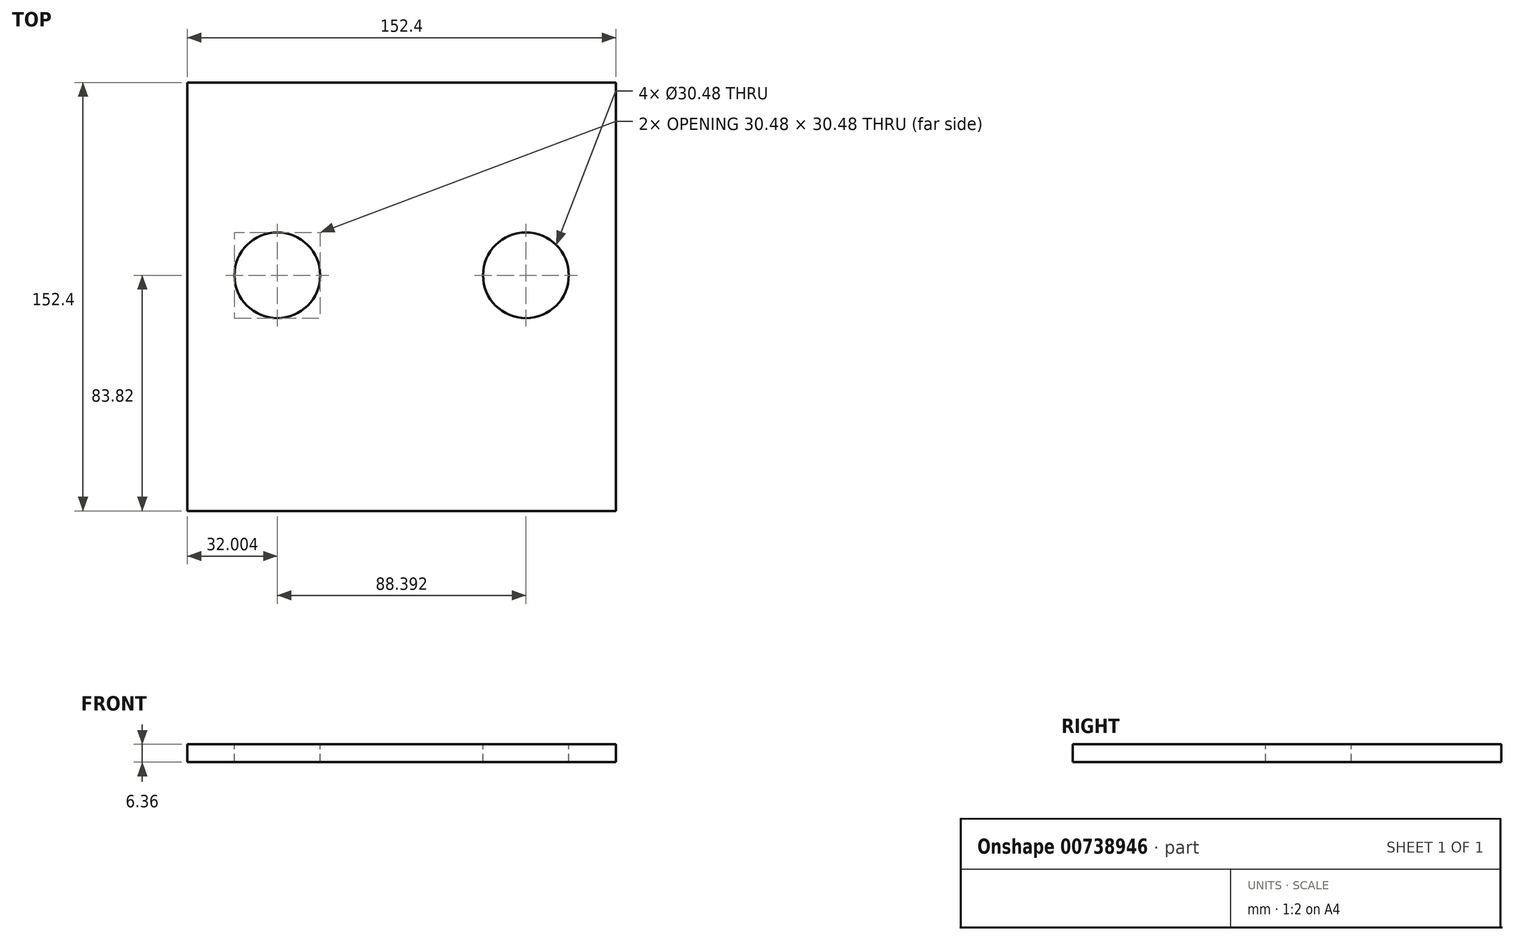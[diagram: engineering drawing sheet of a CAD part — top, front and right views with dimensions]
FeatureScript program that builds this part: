
annotation { "Feature Type Name" : "Feature", "Feature Type Description" : "" }
export const myFeature = defineFeature(function(context is Context, id is Id, definition is map)
    precondition{}
    {
        {
            var Q0;
            Q0=qCreatedBy(makeId("Front.planeOp"),FACE);
            var sketch = newSketch(context, id + "F0", { "sketchPlane" : qUnion([Q0])});
            skLineSegment(sketch, "E0.bottom", {"start": v(76.2, -3.17) * mm, "end": v(-76.2, -3.18) * mm});
            skLineSegment(sketch, "E0.top", {"start": v(76.2, 3.18) * mm, "end": v(-76.2, 3.17) * mm});
            skLineSegment(sketch, "E0.left", {"start": v(76.2, -3.17) * mm, "end": v(76.2, 3.18) * mm});
            skLineSegment(sketch, "E0.right", {"start": v(-76.2, -3.18) * mm, "end": v(-76.2, 3.17) * mm});
            skPoint(sketch, "E0.middle", {"position": v(0, 0) * mm});
            skSolve(sketch);
        }
        {
            var Q0;
            Q0=makeQuery(id+"F0.imprint","IMPRINT",FACE,{"disambiguationData":[TD([[makeQuery(id+"F0.imprint","IMPRINT",EDGE,{"derivedFrom":sQuery(id+"F0.wireOp",EDGE,"E0.bottom")}),-1.0]])]});
            extrude(context, id + "F1", {"entities" : qUnion([Q0]), "depth" : 152.4 * mm, "offsetDistance" : 25.4 * mm});
        }
        {
            var Q0;
            Q0=makeQuery(id+"F1.opExtrude","SWEPT_FACE",FACE,{"disambiguationData":[OSD([sQuery(id+"F0.wireOp",EDGE,"E0.top")])]});
            var sketch = newSketch(context, id + "F2", { "sketchPlane" : qUnion([Q0])});
            skPoint(sketch, "E1", {"position": v(-44.2, -68.58) * mm});
            skLineSegment(sketch, "E2", {"start": v(-44.2, -68.58) * mm, "end": v(-44.2, -152.4) * mm});
            skPoint(sketch, "E3", {"position": v(44.2, -68.58) * mm});
            skLineSegment(sketch, "E4", {"start": v(-44.2, -68.58) * mm, "end": v(44.2, -68.58) * mm});
            skLineSegment(sketch, "E5", {"start": v(44.2, -68.58) * mm, "end": v(44.2, -152.4) * mm});
            skLineSegment(sketch, "E6", {"start": v(-44.2, -68.58) * mm, "end": v(-76.2, -68.58) * mm});
            skLineSegment(sketch, "E7", {"start": v(44.2, -68.58) * mm, "end": v(76.2, -68.58) * mm});
            skPoint(sketch, "E8", {"position": v(0, -68.58) * mm});
            skSolve(sketch);
        }
        {
            var Q0;
            Q0=sQuery(id+"F2.wireOp",VERTEX,"E1");
            var Q1;
            Q1=sQuery(id+"F2.wireOp",VERTEX,"E3");
            var Q2;
            Q2=makeQuery(id+"F1.opExtrude","SWEPT_BODY",BODY,{"disambiguationData":[OSD([sQuery(id+"F0.wireOp",EDGE,"E0.bottom"),sQuery(id+"F0.wireOp",EDGE,"E0.top"),sQuery(id+"F0.wireOp",EDGE,"E0.left"),sQuery(id+"F0.wireOp",EDGE,"E0.right")])]});
            hole(context, id + "F3", {"style" : HoleStyle.SIMPLE, "endStyle" : HoleEndStyle.THROUGH, "holeDiameter" : 30.48 * mm, "majorDiameter" : 6.35 * mm, "isTappedThrough" : true, "tappedDepth" : 12.7 * mm, "tapClearance" : 3, "locations" : qUnion([Q0, Q1]), "scope" : qUnion([Q2])});
        }
        {
            var Q0;
            Q0=makeQuery(id+"F1.opExtrude","SWEPT_BODY",BODY,{"disambiguationData":[OSD([sQuery(id+"F0.wireOp",EDGE,"E0.bottom"),sQuery(id+"F0.wireOp",EDGE,"E0.top"),sQuery(id+"F0.wireOp",EDGE,"E0.left"),sQuery(id+"F0.wireOp",EDGE,"E0.right")])]});
            transform(context, id + "F4", {"entities" : qUnion([Q0]), "transformType" : TransformType.TRANSLATION_3D, "dx" : 0 * mm, "dy" : 0 * mm, "dz" : 0 * mm, "makeCopy" : true});
        }
    });
